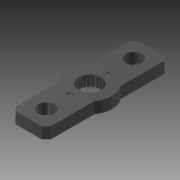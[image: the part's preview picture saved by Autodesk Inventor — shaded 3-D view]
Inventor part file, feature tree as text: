
AUTODESK INVENTOR PART (.ipt)
format: ipt  version: 2013 (Build 170138000, 138)  size: 402,944 bytes
history: native  units: in
note: dims shown in document units (in); Inventor stores cm internally (conversion verified against a paired STEP export)
features: extrude x4, sketch x2, hole x1
ambient origin geometry x8: Origin, YZ Plane, XZ Plane, XY Plane, X Axis, Y Axis, Z Axis, Center Point
bodies: Solid1 (feature_tree)
feature tree (7):
  sketch  "Sketch1"  dims[d0=0.125in d1=0.0137in]
  extrude  "Extrusion1"  Depth=0.01in TaperAngle=0.0deg
  hole  "Hole1"  [1 undecoded]
  extrude  "Extrusion2"  Depth=0.066in TaperAngle=0.0deg
  extrude  "Extrusion3"  [1 undecoded]
  extrude  "Extrusion4"  [1 undecoded]
  sketch  "Sketch2"  dims[d2=0.182in d3=0.75in d4=0.375in d5=0.25in d6=0.5635in d7=1.0in d8=0.8108in d9=0.01in d10=0.0in d11=0.0in d12=0.0137in d13=0.066in d14=0.0in]
note: 3 required parameter values undecoded (feature->parameter linkage not recoverable at this tier; creation-order binding heuristic only, values carry confidence <= 0.55)
